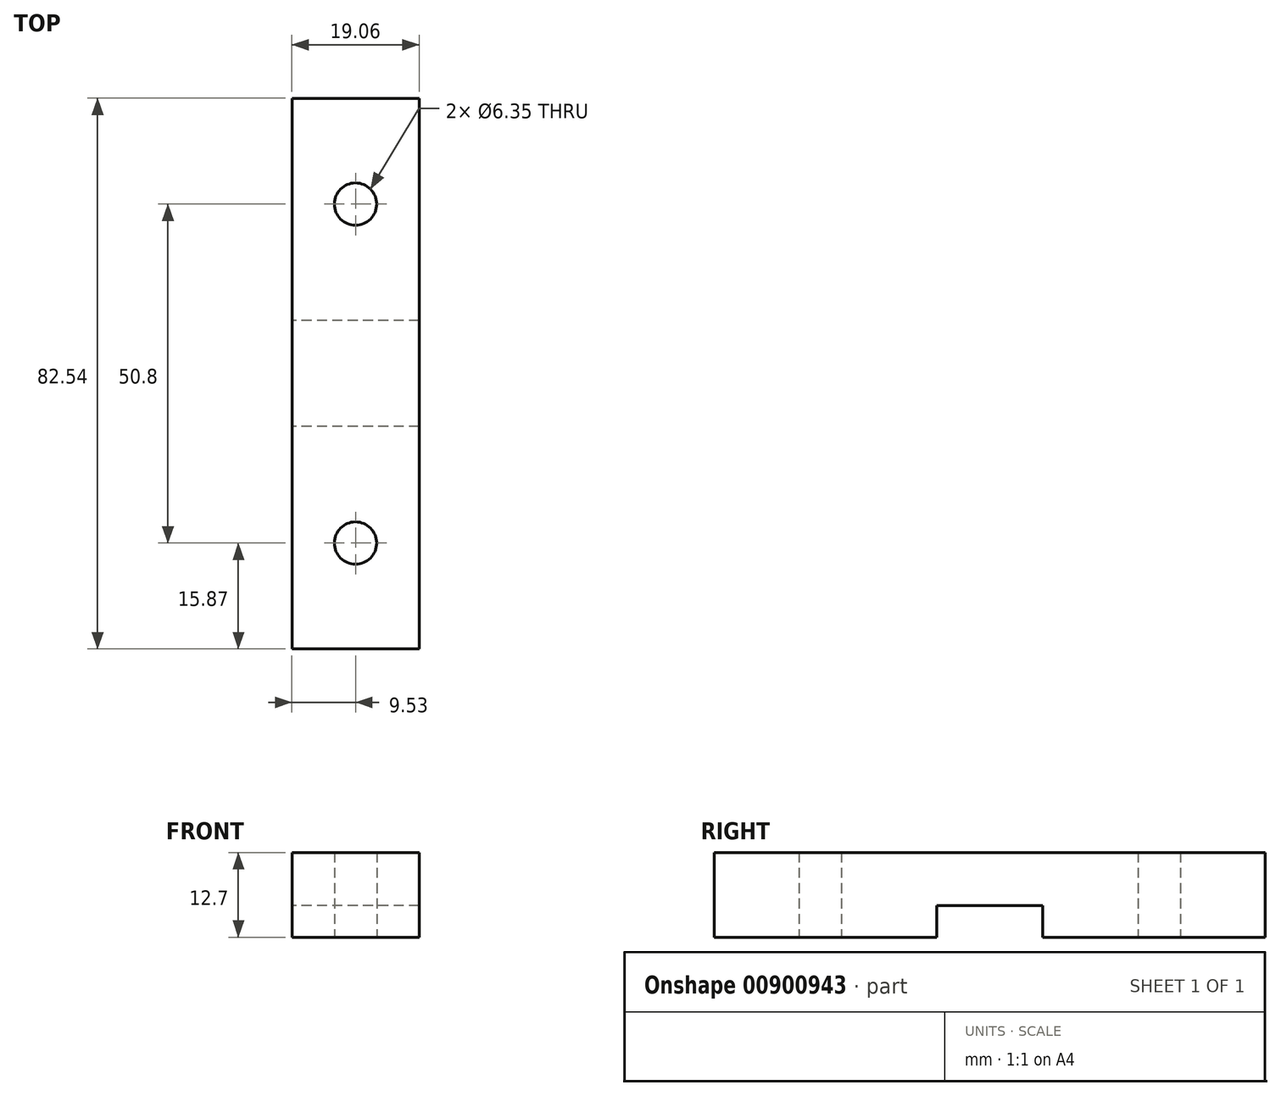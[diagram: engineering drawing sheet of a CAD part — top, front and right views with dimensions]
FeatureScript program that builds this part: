
annotation { "Feature Type Name" : "Feature", "Feature Type Description" : "" }
export const myFeature = defineFeature(function(context is Context, id is Id, definition is map)
    precondition{}
    {
        {
            var Q0;
            Q0=qCreatedBy(makeId("Top.planeOp"),FACE);
            var sketch = newSketch(context, id + "F0", { "sketchPlane" : qUnion([Q0])});
            skLineSegment(sketch, "E0.bottom", {"start": v(9.52, -41.27) * mm, "end": v(-9.53, -41.27) * mm});
            skLineSegment(sketch, "E0.top", {"start": v(9.53, 41.27) * mm, "end": v(-9.52, 41.27) * mm});
            skLineSegment(sketch, "E0.left", {"start": v(9.52, -41.27) * mm, "end": v(9.53, 41.27) * mm});
            skLineSegment(sketch, "E0.right", {"start": v(-9.53, -41.27) * mm, "end": v(-9.52, 41.27) * mm});
            skPoint(sketch, "E0.middle", {"position": v(0, 0) * mm});
            skCircle(sketch, "E1", {"center": v(0, 25.4) * mm, "radius": 3.18 * mm});
            skCircle(sketch, "E2.MirrorC", {"center": v(0, -25.4) * mm, "radius": 3.18 * mm});
            skSolve(sketch);
        }
        {
            var Q0;
            Q0 = qSketchRegion(id + "F0", true);
            extrude(context, id + "F1", {"entities" : qUnion([Q0]), "depth" : 12.7 * mm, "offsetDistance" : 25.4 * mm});
        }
        {
            var Q0;
            Q0=makeQuery(id+"F1.opExtrude","SWEPT_FACE",FACE,{"disambiguationData":[OSD([sQuery(id+"F0.wireOp",EDGE,"E0.right")])]});
            var sketch = newSketch(context, id + "F2", { "sketchPlane" : qUnion([Q0])});
            skLineSegment(sketch, "E3.bottom", {"start": v(7.94, 4.76) * mm, "end": v(-7.94, 4.76) * mm});
            skLineSegment(sketch, "E3.top", {"start": v(7.94, -4.76) * mm, "end": v(-7.94, -4.76) * mm});
            skLineSegment(sketch, "E3.left", {"start": v(7.94, 4.76) * mm, "end": v(7.94, -4.76) * mm});
            skLineSegment(sketch, "E3.right", {"start": v(-7.94, 4.76) * mm, "end": v(-7.94, -4.76) * mm});
            skPoint(sketch, "E3.middle", {"position": v(0, 0) * mm});
            skSolve(sketch);
        }
        {
            var Q0;
            Q0 = qSketchRegion(id + "F2", true);
            extrude(context, id + "F3", {"entities" : qUnion([Q0]), "operationType" : NewBodyOperationType.REMOVE, "endBound" : BoundingType.THROUGH_ALL, "oppositeDirection" : true, "depth" : 25.4 * mm, "offsetDistance" : 25.4 * mm});
        }
    });
